# Revit family: 90001575_BIM
name_source: partatom
category: Mechanical Equipment
units: mm (PartAtom-declared; Revit-internal decimal feet)

## family parameters
Always vertical = Yes
Cut with Voids When Loaded = No
Maintain Annotation Orientation = No
OmniClass Number = 23.75.70.21.31
OmniClass Title = Exhaust Terminals
Part Type = Normal
Room Calculation Point = No
Round Connector Dimension = Use Radius
Shared = No
Work Plane-Based = No

## types (1)
- 90001575
    Article Description = Exhaust Unit
    Article Type = ExhaustUnit MVS-15
    Blue = Color RGB 0-168-255
    Custom = No
    Dark Grey = Color RGB 59-56-56
    Default Elevation = 0 mm  [stored 0 ft]
    Depth = 303 mm  [stored 0.994094 ft]
    Description = Exhaust Unit
    EMCS Version = 2.0
    ETIM Article Class = EC010004
    Family Version = 11.14
    Height = 389 mm  [stored 1.27625 ft]
    HeightPlenum = 463 mm  [stored 1.51903 ft]
    IFCExportAs = IfcAirTerminalBoxType
    IFCExportType = NOTDEFINED
    Light Grey = Color RGB 214-214-214
    MEPcontent Class = EXHAUST_UNIT
    Manufacturer Art. No. = 90001575
    Max_Air_Flow = 127.0 L/s
    Model = ExhaustUnit MVS-15
    Power = 0 VA
    Product Line = Airflow
    Revit Version = 2022
    Voltage = 230 V
    Width = 449 mm  [stored 1.4731 ft]

note: [stored X ft] marks values corroborated as IEEE doubles in the binary element streams (Revit-internal decimal feet)

## geometry (parser evidence)
native form markers: Blend x4, Sweep x1
no freeform markers — native parametric forms only
